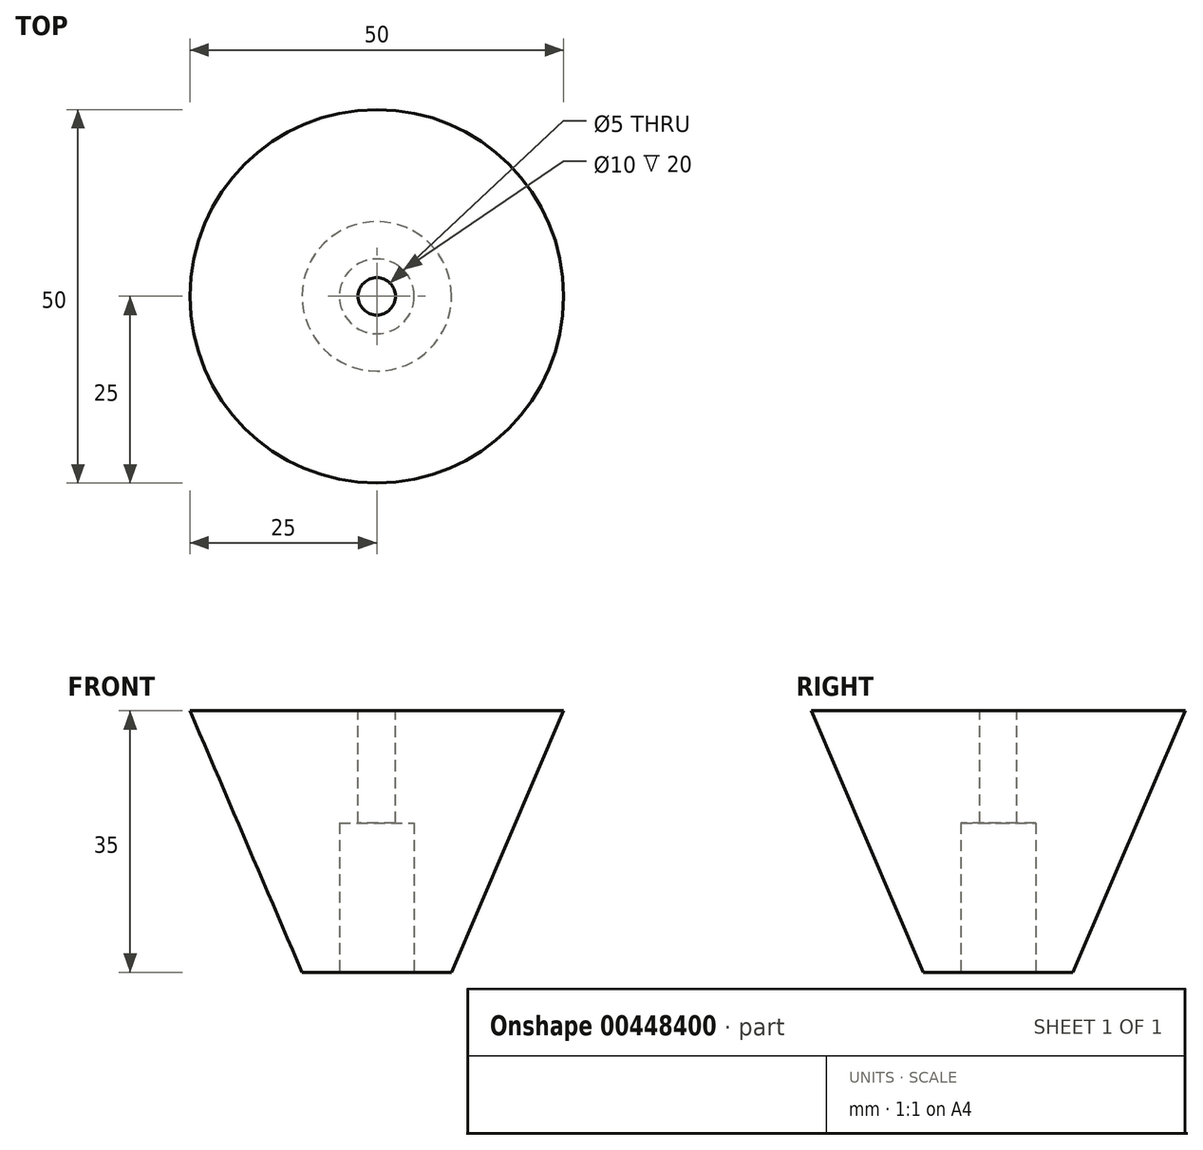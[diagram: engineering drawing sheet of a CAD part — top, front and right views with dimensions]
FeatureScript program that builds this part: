
annotation { "Feature Type Name" : "Feature", "Feature Type Description" : "" }
export const myFeature = defineFeature(function(context is Context, id is Id, definition is map)
    precondition{}
    {
        {
            var Q0;
            Q0=qCreatedBy(makeId("Right.planeOp"),FACE);
            var sketch = newSketch(context, id + "F0", { "sketchPlane" : qUnion([Q0])});
            skLineSegment(sketch, "E0", {"start": v(0, 0) * mm, "end": v(25, 0) * mm});
            skLineSegment(sketch, "E1", {"start": v(25, 0) * mm, "end": v(10, -35) * mm});
            skLineSegment(sketch, "E2", {"start": v(10, -35) * mm, "end": v(0, -35) * mm});
            skLineSegment(sketch, "E3", {"start": v(0, -35) * mm, "end": v(0, 0) * mm});
            skSolve(sketch);
        }
        {
            var Q0;
            Q0=makeQuery(id+"F0.imprint","IMPRINT",FACE,{"disambiguationData":[TD([[makeQuery(id+"F0.imprint","IMPRINT",EDGE,{"derivedFrom":sQuery(id+"F0.wireOp",EDGE,"E0")}),-1.0]])]});
            var Q1;
            Q1=sQuery(id+"F0.wireOp",EDGE,"E3");
            revolve(context, id + "F1", {"entities" : qUnion([Q0]), "axis" : qUnion([Q1]), "revolveType" : RevolveType.ONE_DIRECTION, "angle" : 360 * degree});
        }
        {
            var Q0;
            Q0=makeQuery(id+"F1.opRevolve","SWEPT_FACE",FACE,{"disambiguationData":[OSD([sQuery(id+"F0.wireOp",EDGE,"E0")])]});
            var sketch = newSketch(context, id + "F2", { "sketchPlane" : qUnion([Q0])});
            skCircle(sketch, "E4", {"center": v(0, 0) * mm, "radius": 2.5 * mm});
            skSolve(sketch);
        }
        {
            var Q0;
            Q0=makeQuery(id+"F2.imprint","IMPRINT",FACE,{"disambiguationData":[TD([[makeQuery(id+"F2.imprint","IMPRINT",EDGE,{"derivedFrom":sQuery(id+"F2.wireOp",EDGE,"E4")}),1.0]])]});
            extrude(context, id + "F3", {"entities" : qUnion([Q0]), "operationType" : NewBodyOperationType.REMOVE, "endBound" : BoundingType.THROUGH_ALL, "oppositeDirection" : true, "depth" : 25 * mm});
        }
        {
            var Q0;
            Q0=makeQuery(id+"F1.opRevolve","SWEPT_FACE",FACE,{"disambiguationData":[OSD([sQuery(id+"F0.wireOp",EDGE,"E2")])]});
            var sketch = newSketch(context, id + "F4", { "sketchPlane" : qUnion([Q0])});
            skCircle(sketch, "E5", {"center": v(0, 0) * mm, "radius": 5 * mm});
            skSolve(sketch);
        }
        {
            var Q0;
            Q0=makeQuery(id+"F4.imprint","IMPRINT",FACE,{"disambiguationData":[TD([[makeQuery(id+"F4.imprint","IMPRINT",EDGE,{"derivedFrom":sQuery(id+"F4.wireOp",EDGE,"E5")}),1.0]])]});
            extrude(context, id + "F5", {"entities" : qUnion([Q0]), "operationType" : NewBodyOperationType.REMOVE, "oppositeDirection" : true, "depth" : 20 * mm});
        }
    });
